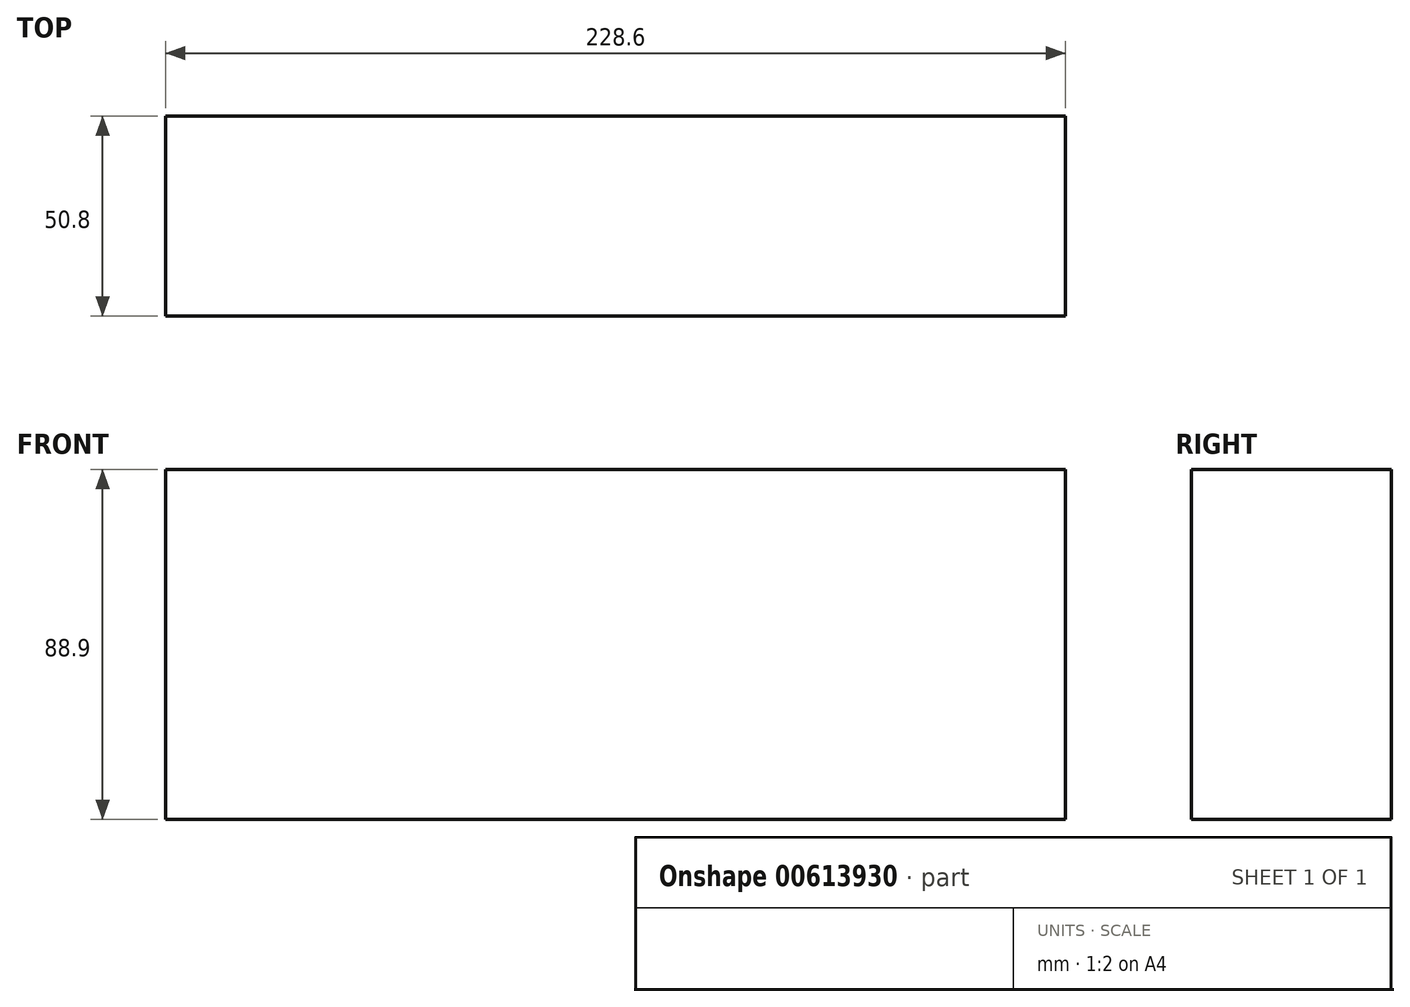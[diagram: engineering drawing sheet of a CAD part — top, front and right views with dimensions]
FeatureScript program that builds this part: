
annotation { "Feature Type Name" : "Feature", "Feature Type Description" : "" }
export const myFeature = defineFeature(function(context is Context, id is Id, definition is map)
    precondition{}
    {
        {
            var Q0;
            Q0=qCreatedBy(makeId("Top.planeOp"),FACE);
            var sketch = newSketch(context, id + "F0", { "sketchPlane" : qUnion([Q0])});
            skLineSegment(sketch, "E0.bottom", {"start": v(-67.02, 26.98) * mm, "end": v(161.58, 26.98) * mm});
            skLineSegment(sketch, "E0.top", {"start": v(-67.02, -23.82) * mm, "end": v(161.58, -23.82) * mm});
            skLineSegment(sketch, "E0.left", {"start": v(-67.02, 26.98) * mm, "end": v(-67.02, -23.82) * mm});
            skLineSegment(sketch, "E0.right", {"start": v(161.58, 26.98) * mm, "end": v(161.58, -23.82) * mm});
            skSolve(sketch);
        }
        {
            var Q0;
            Q0 = qSketchRegion(id + "F0", true);
            extrude(context, id + "F1", {"entities" : qUnion([Q0]), "depth" : 88.9 * mm, "offsetDistance" : 25.4 * mm});
        }
    });
